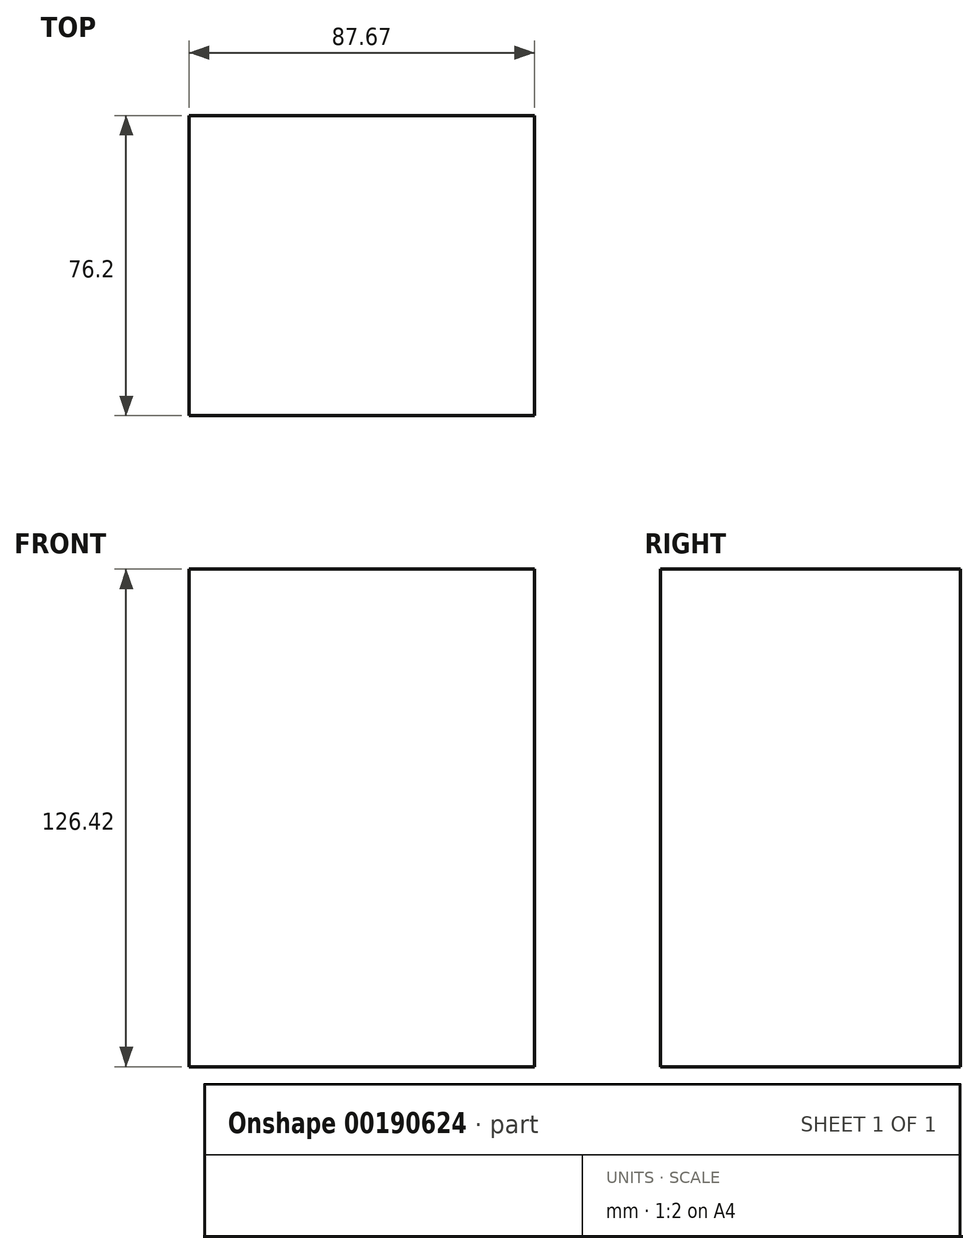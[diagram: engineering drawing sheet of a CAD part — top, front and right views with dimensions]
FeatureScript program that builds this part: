
annotation { "Feature Type Name" : "Feature", "Feature Type Description" : "" }
export const myFeature = defineFeature(function(context is Context, id is Id, definition is map)
    precondition{}
    {
        {
            var Q0;
            Q0=qCreatedBy(makeId("Front.planeOp"),FACE);
            var sketch = newSketch(context, id + "F0", { "sketchPlane" : qUnion([Q0])});
            skLineSegment(sketch, "E0.bottom", {"start": v(-43.16, 63.7) * mm, "end": v(44.51, 63.7) * mm});
            skLineSegment(sketch, "E0.top", {"start": v(-43.16, -62.73) * mm, "end": v(44.51, -62.73) * mm});
            skLineSegment(sketch, "E0.left", {"start": v(-43.16, 63.7) * mm, "end": v(-43.16, -62.73) * mm});
            skLineSegment(sketch, "E0.right", {"start": v(44.51, 63.7) * mm, "end": v(44.51, -62.73) * mm});
            skLineSegment(sketch, "E1.bottom", {"start": v(-43.16, 63.7) * mm, "end": v(44.5, 63.7) * mm});
            skLineSegment(sketch, "E1.top", {"start": v(-43.16, 75.33) * mm, "end": v(44.5, 75.33) * mm});
            skLineSegment(sketch, "E1.left", {"start": v(-43.16, 63.7) * mm, "end": v(-43.16, 75.33) * mm});
            skLineSegment(sketch, "E1.right", {"start": v(44.5, 63.7) * mm, "end": v(44.5, 75.33) * mm});
            skSolve(sketch);
        }
        {
            var Q0;
            Q0=makeQuery(id+"F0.imprint","IMPRINT",FACE,{"disambiguationData":[TD([[makeQuery(id+"F0.imprint","IMPRINT",EDGE,{"derivedFrom":sQuery(id+"F0.wireOp",EDGE,"E0.bottom")}),-1.0]])]});
            extrude(context, id + "F1", {"entities" : qUnion([Q0]), "depth" : 76.2 * mm});
        }
    });
